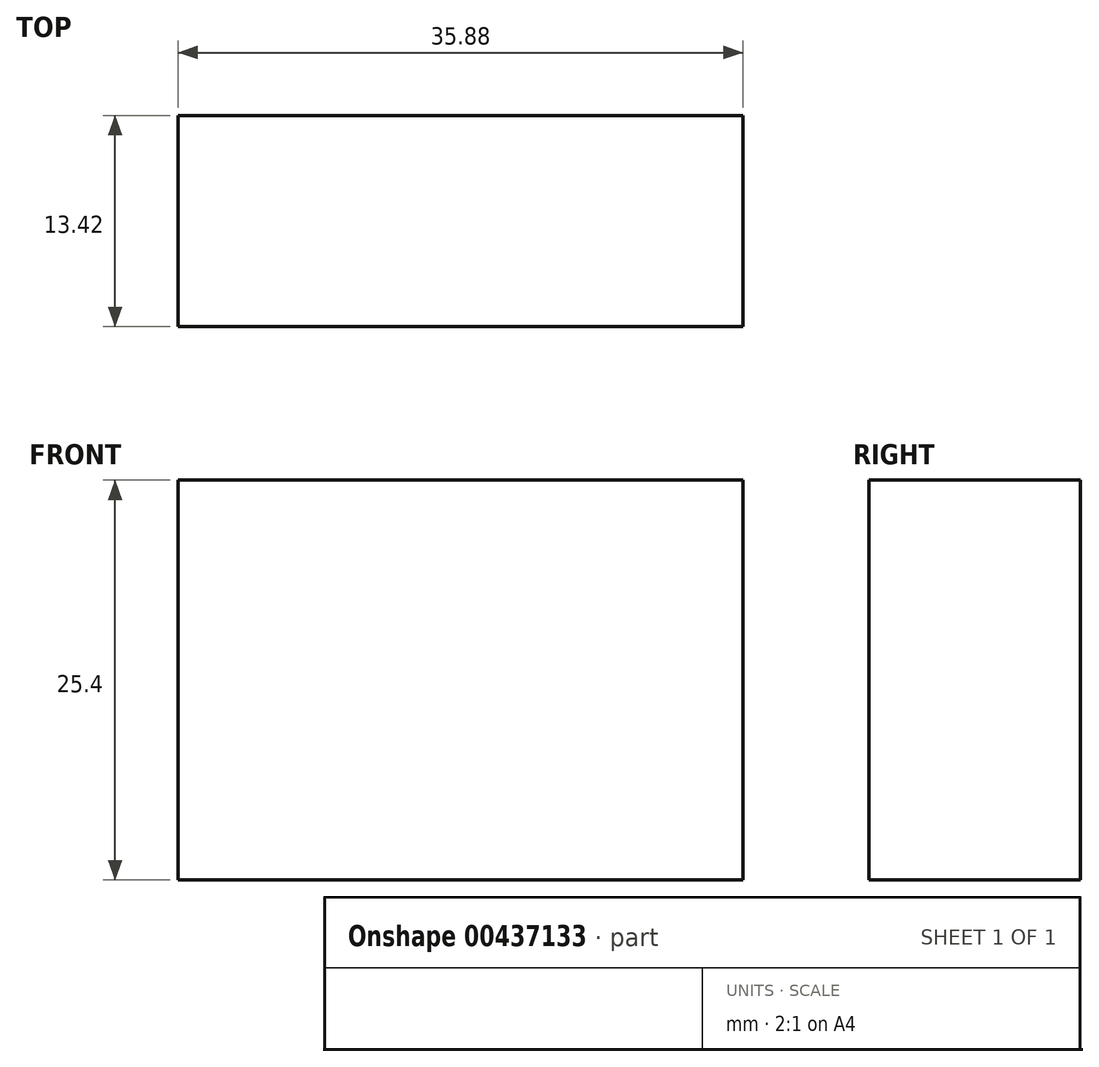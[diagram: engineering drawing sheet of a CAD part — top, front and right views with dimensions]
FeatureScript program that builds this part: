
annotation { "Feature Type Name" : "Feature", "Feature Type Description" : "" }
export const myFeature = defineFeature(function(context is Context, id is Id, definition is map)
    precondition{}
    {
        {
            var Q0;
            Q0=qCreatedBy(makeId("Top.planeOp"),FACE);
            var sketch = newSketch(context, id + "F0", { "sketchPlane" : qUnion([Q0])});
            skLineSegment(sketch, "E0.bottom", {"start": v(0, 13.42) * mm, "end": v(35.88, 13.42) * mm});
            skLineSegment(sketch, "E0.top", {"start": v(0, 0) * mm, "end": v(35.88, 0) * mm});
            skLineSegment(sketch, "E0.left", {"start": v(0, 13.42) * mm, "end": v(0, 0) * mm});
            skLineSegment(sketch, "E0.right", {"start": v(35.88, 13.42) * mm, "end": v(35.88, 0) * mm});
            skSolve(sketch);
        }
        {
            var Q0;
            Q0=makeQuery(id+"F0.imprint","IMPRINT",FACE,{"disambiguationData":[TD([[makeQuery(id+"F0.imprint","IMPRINT",EDGE,{"derivedFrom":sQuery(id+"F0.wireOp",EDGE,"E0.bottom")}),-1.0]])]});
            extrude(context, id + "F1", {"entities" : qUnion([Q0]), "depth" : 25.4 * mm});
        }
    });
